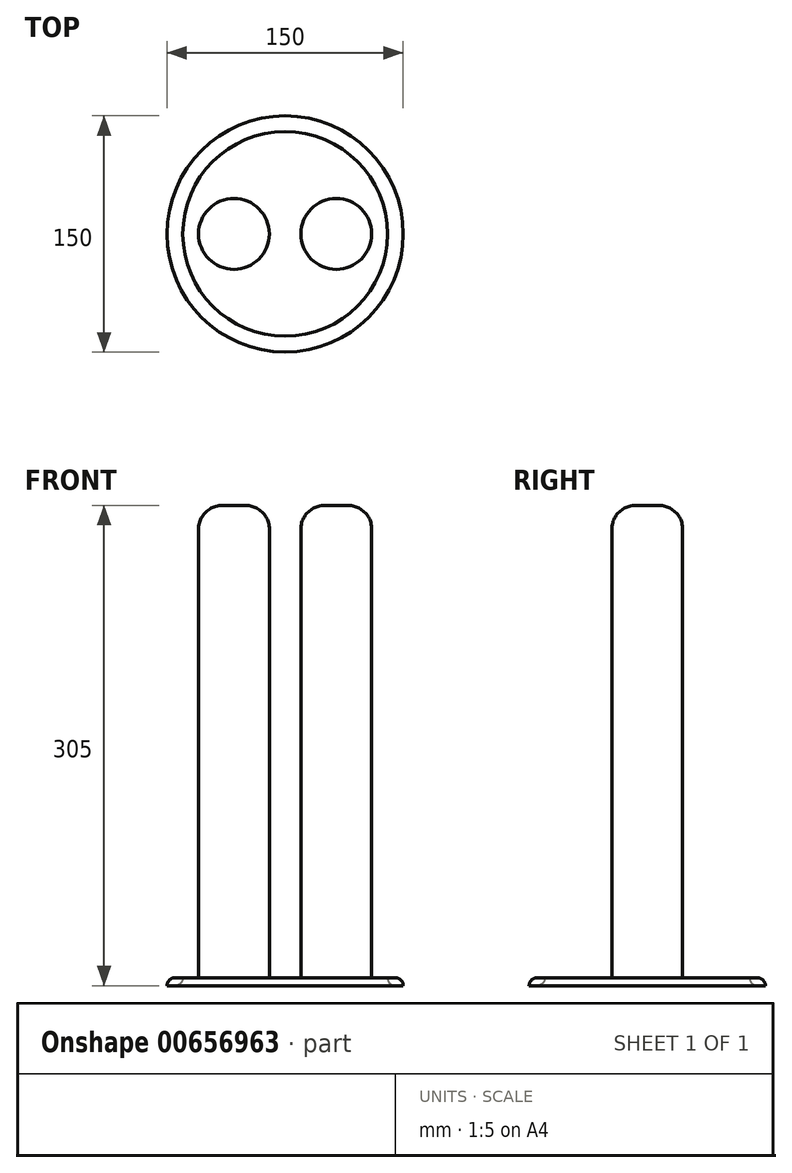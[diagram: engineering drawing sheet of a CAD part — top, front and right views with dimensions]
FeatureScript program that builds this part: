
annotation { "Feature Type Name" : "Feature", "Feature Type Description" : "" }
export const myFeature = defineFeature(function(context is Context, id is Id, definition is map)
    precondition{}
    {
        {
            var Q0;
            Q0=qCreatedBy(makeId("Top.planeOp"),FACE);
            var sketch = newSketch(context, id + "F0", { "sketchPlane" : qUnion([Q0])});
            skCircle(sketch, "E0", {"center": v(0, 0) * mm, "radius": 75 * mm});
            skCircle(sketch, "E1.0", {"center": v(0, 0) * mm, "radius": 65 * mm});
            skSolve(sketch);
        }
        {
            var Q0;
            Q0=makeQuery(id+"F0.imprint","IMPRINT",FACE,{"disambiguationData":[TD([[makeQuery(id+"F0.imprint","IMPRINT",EDGE,{"derivedFrom":sQuery(id+"F0.wireOp",EDGE,"E0")}),1.0]])]});
            extrude(context, id + "F1", {"entities" : qUnion([Q0]), "depth" : 5 * mm, "offsetDistance" : 25 * mm});
        }
        {
            var Q0;
            Q0=makeQuery(id+"F1.opExtrude","CAP_EDGE",EDGE,{"disambiguationData":[OSD([sQuery(id+"F0.wireOp",EDGE,"E0")])],"isStart":false});
            var Q1;
            Q1=makeQuery(id+"F1.opExtrude","CAP_EDGE",EDGE,{"disambiguationData":[OSD([sQuery(id+"F0.wireOp",EDGE,"E1.0")])],"isStart":true});
            fillet(context, id + "F2", {"entities" : qUnion([Q0, Q1]), "radius" : 5 * mm, "tangentPropagation" : true, "allowEdgeOverflow" : false});
        }
        {
            var Q0;
            Q0=makeQuery(id+"F1.opExtrude","CAP_FACE",FACE,{"disambiguationData":[OSD([sQuery(id+"F0.wireOp",EDGE,"E0"),sQuery(id+"F0.wireOp",EDGE,"E1.0")])],"isStart":false});
            var sketch = newSketch(context, id + "F3", { "sketchPlane" : qUnion([Q0])});
            skLineSegment(sketch, "E2", {"start": v(-65, 0) * mm, "end": v(-55, 0) * mm});
            skLineSegment(sketch, "E3", {"start": v(0, 0) * mm, "end": v(10, 0) * mm});
            skCircle(sketch, "E4", {"center": v(-32.5, 0) * mm, "radius": 22.5 * mm});
            skCircle(sketch, "E5", {"center": v(32.5, 0) * mm, "radius": 22.5 * mm});
            skLineSegment(sketch, "E6.trimOffspring", {"start": v(-10, 0) * mm, "end": v(0, 0) * mm});
            skLineSegment(sketch, "E7.trimOffspring", {"start": v(55, 0) * mm, "end": v(65, 0) * mm});
            skSolve(sketch);
        }
        {
            var Q0;
            {var subQ0=sQuery(id+"F3.wireOp",EDGE,"E4");var subQ1=makeQuery(id+"F3.imprint","INTERSECT",VERTEX,{"derivedFrom":[sQuery(id+"F3.wireOp",EDGE,"E2"),subQ0]});Q0=makeQuery(id+"F3.imprint","IMPRINT",FACE,{"disambiguationData":[TD([[makeQuery(id+"F3.imprint","IMPRINT",EDGE,{"disambiguationData":[TD([[subQ1,1.0]])],"derivedFrom":subQ0}),1.0]])]});}
            var Q1;
            {var subQ0=sQuery(id+"F3.wireOp",EDGE,"E5");var subQ1=makeQuery(id+"F3.imprint","INTERSECT",VERTEX,{"derivedFrom":[sQuery(id+"F3.wireOp",EDGE,"E3"),subQ0]});Q1=makeQuery(id+"F3.imprint","IMPRINT",FACE,{"disambiguationData":[TD([[makeQuery(id+"F3.imprint","IMPRINT",EDGE,{"disambiguationData":[TD([[subQ1,1.0]])],"derivedFrom":subQ0}),1.0]])]});}
            extrude(context, id + "F4", {"entities" : qUnion([Q0, Q1]), "depth" : 300 * mm, "offsetDistance" : 25 * mm});
        }
        {
            var Q0;
            Q0=makeQuery(id+"F4.opExtrude","CAP_FACE",FACE,{"disambiguationData":[OSD([sQuery(id+"F3.wireOp",EDGE,"E5")])],"isStart":false});
            var Q1;
            Q1=makeQuery(id+"F4.opExtrude","CAP_EDGE",EDGE,{"disambiguationData":[OSD([sQuery(id+"F3.wireOp",EDGE,"E4")])],"isStart":false});
            fillet(context, id + "F5", {"entities" : qUnion([Q0, Q1]), "radius" : 15 * mm, "tangentPropagation" : true, "allowEdgeOverflow" : false});
        }
    });
